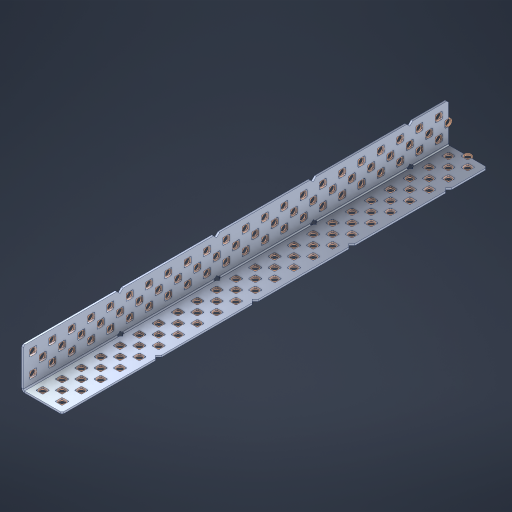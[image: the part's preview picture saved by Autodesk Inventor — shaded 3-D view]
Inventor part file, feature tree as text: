
AUTODESK INVENTOR PART (.ipt)
format: ipt  version: 2023 (Build 270158000, 158)  size: 1,645,568 bytes
history: native  units: in
note: dims shown in document units (in); Inventor stores cm internally (conversion verified against a paired STEP export)
features: other x138, extrude x130, sheet_metal_op x8, sketch x7, pattern_linear x2, mirror x1, chamfer x1
ambient origin geometry x8: Origin, YZ Plane, XZ Plane, XY Plane, X Axis, Y Axis, Z Axis, Center Point
bodies: Solid1 (feature_tree), Body (feature_tree)
feature tree (287):
  sheet_metal_op  "Flanges"
  sheet_metal_op  "Body Pattern"
  pattern_linear  "Center Pattern"  Spacing1=1.0in  [1 undecoded]
  other  "Arc Length"
  pattern_linear  "Notch Pattern"  Spacing1=0.1875in  [1 undecoded]
  other  "Diagonal Plane"
  mirror  "Everything Mirrored"
  chamfer  "End Chamfer"
  sketch  "Sketch1"  dims[d0=1.0in]
  other  "Plate1"
  sketch  "Sketch2"  dims[d1=11.0in]
  other  "Plate2"
  sheet_metal_op  "Bend1"
  sheet_metal_op  "Corner1"
  sketch  "Sketch8"  dims[d2=0.0469in]
  sketch  "Sketch9"  dims[d3=0.0469in]
  other  "Srf91"
  sheet_metal_op  "Body Pattern Sketch"
  other  "Srf92"
  sketch  "Sketch13"  dims[d4=0.0234in]
  sketch  "Sketch15"  dims[d5=0.0938in]
  sketch  "Sketch16"  dims[d6=0.0469in d7=1.0in d8=90.0deg d9=0.0312in d10=0.1875in d11=0.0469in d12=0.0469in d49=0.182in d50=0.02in d52=0.25in d53=0.0469in d54=0.0in d55=0.172in d56=1.0in d57=0.0in d60=8.6614in d62=0.5in d63=0.7874in d65=0.5in d85=0.1473in d86=0.1659in d89=0.0469in d90=0.0in d91=0.04in d92=0.0491in d95=2.5in d96=0.04in d97=0.25in d98=45.0deg d99=0.25in d106=0.182in d107=0.02in d108=0.5in d110=0.0469in d111=0.0in d112=0.172in d113=0.5in d114=0.0in d117=0.5in d123=0.25in d125=0.25in d126=0.0491in d127=0.1227in d128=0.08in d129=0.04in d130=2.5in]
  other  "Srf786"
  other  "Srf856"
  other  "Srf857"
  other  "Srf858"
  other  "Srf859"
  other  "Srf860"
  other  "Srf861"
  other  "Srf889"
  other  "Srf890"
  other  "Srf891"
  other  "Srf1275"
  other  "Srf1276"
  other  "Srf1278"
  other  "Srf1279"
  other  "Srf1280"
  other  "Srf1281"
  other  "Srf1282"
  other  "Srf1283"
  other  "Srf1277"
  other  "Srf1285"
  other  "Srf1286"
  other  "Srf1287"
  other  "Srf1383"
  other  "Srf1384"
  other  "Srf1385"
  other  "Srf1386"
  other  "Srf1387"
  other  "Srf1388"
  other  "Srf1389"
  other  "Srf1390"
  other  "Srf1391"
  other  "Srf1392"
  other  "Srf1393"
  other  "Srf1394"
  other  "Srf1395"
  other  "Srf1396"
  other  "Srf1397"
  other  "Srf1398"
  other  "Srf1399"
  other  "Srf1400"
  other  "Srf1401"
  other  "Srf1402"
  other  "Srf1403"
  other  "Srf1404"
  other  "Srf1405"
  other  "Srf1406"
  other  "Srf1407"
  other  "Srf1408"
  other  "Srf1409"
  other  "Srf1410"
  other  "Srf1411"
  other  "Srf1412"
  other  "Srf1413"
  other  "Srf1414"
  other  "Srf1415"
  other  "Srf1416"
  other  "Srf1417"
  other  "Srf1418"
  other  "Srf1445"
  other  "Srf1446"
  other  "Srf1447"
  other  "Srf1448"
  other  "Srf1449"
  other  "Srf1450"
  other  "Srf1451"
  other  "Srf1452"
  other  "Srf1453"
  other  "Srf1454"
  other  "Srf1455"
  other  "Srf1456"
  other  "Srf1457"
  other  "Srf1458"
  other  "Srf1459"
  other  "Srf1460"
  other  "Srf1461"
  other  "Srf1462"
  other  "Srf1475"
  other  "Srf1476"
  other  "Srf1477"
  other  "Srf1478"
  other  "Srf1479"
  other  "Srf1480"
  other  "Srf1481"
  other  "Srf1482"
  other  "Srf1483"
  other  "Srf1484"
  other  "Srf1485"
  other  "Srf1486"
  other  "Srf1487"
  other  "Srf1488"
  other  "Srf1489"
  other  "Srf1490"
  other  "Srf1491"
  other  "Srf1492"
  other  "Srf1493"
  other  "Srf1494"
  other  "Srf1495"
  other  "Srf1496"
  other  "Srf1497"
  other  "Srf1498"
  other  "Srf1499"
  other  "Srf1500"
  other  "Srf1501"
  other  "Srf1502"
  other  "Srf1503"
  other  "Srf1504"
  other  "Srf1505"
  other  "Srf1506"
  other  "Srf1507"
  other  "Srf1508"
  other  "Srf1509"
  other  "Srf1510"
  other  "Srf1537"
  other  "Srf1538"
  other  "Srf1539"
  other  "Srf1540"
  other  "Srf1541"
  other  "Srf1542"
  other  "Srf1543"
  other  "Srf1544"
  other  "Srf1545"
  other  "Srf1546"
  other  "Srf1547"
  other  "Srf1548"
  other  "Srf1549"
  other  "Srf1550"
  other  "Srf1551"
  other  "Srf1552"
  other  "Srf1553"
  other  "Srf1554"
  sheet_metal_op  "Body Stamp"
  sheet_metal_op  "Body Circle"
  other  "Center Stamp"
  other  "Center Circle"
  sheet_metal_op  "Notch"
  extrude  "ExtrusionSrf92"  Depth=0.0469in
  extrude  "ExtrusionSrf856"  Depth=0.0469in
  extrude  "ExtrusionSrf857"  Depth=0.182in
  extrude  "ExtrusionSrf858"  Depth=0.02in
  extrude  "ExtrusionSrf859"  Depth=0.25in
  extrude  "ExtrusionSrf860"  Depth=0.0469in
  extrude  "ExtrusionSrf861"  TaperAngle=0.0deg  [1 undecoded]
  extrude  "ExtrusionSrf889"  Depth=2.5in
  extrude  "ExtrusionSrf890"  Depth=1.0in TaperAngle=0.0deg
  extrude  "ExtrusionSrf891"  Depth=2.5in
  extrude  "ExtrusionSrf1275"  Depth=0.5in
  extrude  "ExtrusionSrf1276"  Depth=2.5in
  extrude  "ExtrusionSrf1277"  Depth=2.5in
  extrude  "ExtrusionSrf1278"  Depth=0.0469in
  extrude  "ExtrusionSrf1279"  Depth=2.5in TaperAngle=0.0deg
  extrude  "ExtrusionSrf1280"  Depth=2.5in
  extrude  "ExtrusionSrf1281"  Depth=0.25in TaperAngle=45.0deg
  extrude  "ExtrusionSrf1282"  Depth=0.25in
  extrude  "ExtrusionSrf1345"  Depth=0.182in
  extrude  "ExtrusionSrf1346"  Depth=0.02in
  extrude  "ExtrusionSrf1347"  Depth=0.5in
  extrude  "ExtrusionSrf1348"  Depth=0.0469in
  extrude  "ExtrusionSrf1383"  TaperAngle=0.0deg  [1 undecoded]
  extrude  "ExtrusionSrf1384"  Depth=2.5in
  extrude  "ExtrusionSrf1385"  Depth=0.5in TaperAngle=0.0deg
  extrude  "ExtrusionSrf1386"  Depth=0.5in
  extrude  "ExtrusionSrf1387"  Depth=0.25in
  extrude  "ExtrusionSrf1388"  Depth=0.25in
  extrude  "ExtrusionSrf1389"  Depth=2.5in
  extrude  "ExtrusionSrf1390"  Depth=2.5in
  extrude  "ExtrusionSrf1391"  Depth=2.5in
  extrude  "ExtrusionSrf1392"  Depth=2.5in
  extrude  "ExtrusionSrf1393"  Depth=2.5in
  extrude  "ExtrusionSrf1394"  [1 undecoded]
  extrude  "ExtrusionSrf1395"  [1 undecoded]
  extrude  "ExtrusionSrf1396"  [1 undecoded]
  extrude  "ExtrusionSrf1397"  [1 undecoded]
  extrude  "ExtrusionSrf1398"  [1 undecoded]
  extrude  "ExtrusionSrf1399"  [1 undecoded]
  extrude  "ExtrusionSrf1400"  [1 undecoded]
  extrude  "ExtrusionSrf1401"  [1 undecoded]
  extrude  "ExtrusionSrf1402"  [1 undecoded]
  extrude  "ExtrusionSrf1403"  [1 undecoded]
  extrude  "ExtrusionSrf1404"  [1 undecoded]
  extrude  "ExtrusionSrf1405"  [1 undecoded]
  extrude  "ExtrusionSrf1406"  [1 undecoded]
  extrude  "ExtrusionSrf1407"  [1 undecoded]
  extrude  "ExtrusionSrf1408"  [1 undecoded]
  extrude  "ExtrusionSrf1409"  [1 undecoded]
  extrude  "ExtrusionSrf1410"  [1 undecoded]
  extrude  "ExtrusionSrf1411"  [1 undecoded]
  extrude  "ExtrusionSrf1412"  [1 undecoded]
  extrude  "ExtrusionSrf1413"  [1 undecoded]
  extrude  "ExtrusionSrf1414"  [1 undecoded]
  extrude  "ExtrusionSrf1415"  [1 undecoded]
  extrude  "ExtrusionSrf1416"  [1 undecoded]
  extrude  "ExtrusionSrf1417"  [1 undecoded]
  extrude  "ExtrusionSrf1418"  [1 undecoded]
  extrude  "ExtrusionSrf1445"  [1 undecoded]
  extrude  "ExtrusionSrf1446"  [1 undecoded]
  extrude  "ExtrusionSrf1447"  [1 undecoded]
  extrude  "ExtrusionSrf1448"  [1 undecoded]
  extrude  "ExtrusionSrf1449"  [1 undecoded]
  extrude  "ExtrusionSrf1450"  [1 undecoded]
  extrude  "ExtrusionSrf1451"  [1 undecoded]
  extrude  "ExtrusionSrf1452"  [1 undecoded]
  extrude  "ExtrusionSrf1453"  [1 undecoded]
  extrude  "ExtrusionSrf1454"  [1 undecoded]
  extrude  "ExtrusionSrf1455"  [1 undecoded]
  extrude  "ExtrusionSrf1456"  [1 undecoded]
  extrude  "ExtrusionSrf1457"  [1 undecoded]
  extrude  "ExtrusionSrf1458"  [1 undecoded]
  extrude  "ExtrusionSrf1459"  [1 undecoded]
  extrude  "ExtrusionSrf1460"  [1 undecoded]
  extrude  "ExtrusionSrf1461"  [1 undecoded]
  extrude  "ExtrusionSrf1462"  [1 undecoded]
  extrude  "ExtrusionSrf1475"  [1 undecoded]
  extrude  "ExtrusionSrf1476"  [1 undecoded]
  extrude  "ExtrusionSrf1477"  [1 undecoded]
  extrude  "ExtrusionSrf1478"  [1 undecoded]
  extrude  "ExtrusionSrf1479"  [1 undecoded]
  extrude  "ExtrusionSrf1480"  [1 undecoded]
  extrude  "ExtrusionSrf1481"  [1 undecoded]
  extrude  "ExtrusionSrf1482"  [1 undecoded]
  extrude  "ExtrusionSrf1483"  [1 undecoded]
  extrude  "ExtrusionSrf1484"  [1 undecoded]
  extrude  "ExtrusionSrf1485"  [1 undecoded]
  extrude  "ExtrusionSrf1486"  [1 undecoded]
  extrude  "ExtrusionSrf1487"  [1 undecoded]
  extrude  "ExtrusionSrf1488"  [1 undecoded]
  extrude  "ExtrusionSrf1489"  [1 undecoded]
  extrude  "ExtrusionSrf1490"  [1 undecoded]
  extrude  "ExtrusionSrf1491"  [1 undecoded]
  extrude  "ExtrusionSrf1492"  [1 undecoded]
  extrude  "ExtrusionSrf1493"  [1 undecoded]
  extrude  "ExtrusionSrf1494"  [1 undecoded]
  extrude  "ExtrusionSrf1495"  [1 undecoded]
  extrude  "ExtrusionSrf1496"  [1 undecoded]
  extrude  "ExtrusionSrf1497"  [1 undecoded]
  extrude  "ExtrusionSrf1498"  [1 undecoded]
  extrude  "ExtrusionSrf1499"  [1 undecoded]
  extrude  "ExtrusionSrf1500"  [1 undecoded]
  extrude  "ExtrusionSrf1501"  [1 undecoded]
  extrude  "ExtrusionSrf1502"  [1 undecoded]
  extrude  "ExtrusionSrf1503"  [1 undecoded]
  extrude  "ExtrusionSrf1504"  [1 undecoded]
  extrude  "ExtrusionSrf1505"  [1 undecoded]
  extrude  "ExtrusionSrf1506"  [1 undecoded]
  extrude  "ExtrusionSrf1507"  [1 undecoded]
  extrude  "ExtrusionSrf1508"  [1 undecoded]
  extrude  "ExtrusionSrf1509"  [1 undecoded]
  extrude  "ExtrusionSrf1510"  [1 undecoded]
  extrude  "ExtrusionSrf1537"  [1 undecoded]
  extrude  "ExtrusionSrf1538"  [1 undecoded]
  extrude  "ExtrusionSrf1539"  [1 undecoded]
  extrude  "ExtrusionSrf1540"  [1 undecoded]
  extrude  "ExtrusionSrf1541"  [1 undecoded]
  extrude  "ExtrusionSrf1542"  [1 undecoded]
  extrude  "ExtrusionSrf1543"  [1 undecoded]
  extrude  "ExtrusionSrf1544"  [1 undecoded]
  extrude  "ExtrusionSrf1545"  [1 undecoded]
  extrude  "ExtrusionSrf1546"  [1 undecoded]
  extrude  "ExtrusionSrf1547"  [1 undecoded]
  extrude  "ExtrusionSrf1548"  [1 undecoded]
  extrude  "ExtrusionSrf1549"  [1 undecoded]
  extrude  "ExtrusionSrf1550"  [1 undecoded]
  extrude  "ExtrusionSrf1551"  [1 undecoded]
  extrude  "ExtrusionSrf1552"  [1 undecoded]
  extrude  "ExtrusionSrf1553"  [1 undecoded]
  extrude  "ExtrusionSrf1554"  [1 undecoded]
note: 101 required parameter values undecoded (feature->parameter linkage not recoverable at this tier; creation-order binding heuristic only, values carry confidence <= 0.55)
